# Revit family: BTD-S
name_source: partatom
category: Communication Devices
revit_build: Autodesk Revit 2014 (Build: 20130308_1515(x64)
units: mm (PartAtom-declared; Revit-internal decimal feet)

## types (1)
- BTD
    Assembly Code = D5090
    Black = Paint - Hubbell - Carbon Black
    Default Elevation = 48 "
    Description = Hubbell Control Solutions' specialty button service provides an easy, customized solution to meet commercial design requirements. The offering includes a list of our most popular text buttons and options to customize the text. Our custom service supports NX, CX and LVS wall stations. The buttons can easily be installed without the need to detach the switch from the wall. Custom text buttons are the ideal solution for any application providing unique control and a personalized experience. All custom specialty button orders require the appropriate product order form to be complted and attached to the order to ensure accuracy.
    Features = Easy to install
1-6 button models with or without light pipe for pilot light functionality
Available for all HCS wall station types: NXSW, CXSW and LVS
Available in White, Gray, Ivory, Light Almond, Black and Red
5pt Arial Narrow
8-character limit using capital letters
Order forms are product specific
Order forms provided to customer service must be in the original editable PDF downloaded from the HCS website (not scanned, handwritten, faxed and not a copy)
5-year warranty
    Light = Yes
    Manufacturer = Hubbell Control Solutions
    Model = Specialty Text Buttons
    Product Documentation Link = https://hubbellcdn.com
    Product Page URL = https://www.hubbell.com
    Type Comments = Text Buttons
    URL = https://www.hubbell.com
    White = Paint - Hubbell - Matte White
    Width = 1.6 "

## geometry (parser evidence)
native form markers: Sweep x1
no freeform markers — native parametric forms only
